# Revit family: Return Screen
name_source: partatom
category: Furniture
units: mm (PartAtom-declared; Revit-internal decimal feet)

## family parameters
Always vertical = Yes
Cut with Voids When Loaded = No
OmniClass Number = 23.40.20.00
OmniClass Title = General Furniture and Specialties
Room Calculation Point = No
Shared = No
Work Plane-Based = No

## types (3) — shared parameters
Assembly Code = E2020200
Manufacturer = Gresham Office Furniture
Model = MIRAGE LITE
Product Data Specification = https://gof.co.uk
Range = SCREENS
Screen = GABRIEL Byron_11101
URL = www.gof.co.uk

## per-type parameters (varying)
| type | Product Code | Width |
| 1000 x 380 High Return Screen | ML1004-R | 1000 mm  [stored 3.28084 ft] |
| 800 x 380 High Return Screen | ML0804-R | 800 mm  [stored 2.62467 ft] |
| 600 x 380 High Return Screen | ML0604-R | 600 mm |

note: [stored X ft] marks values corroborated as IEEE doubles in the binary element streams (Revit-internal decimal feet)

## geometry (parser evidence)
native form markers: Sweep x3
no freeform markers — native parametric forms only
